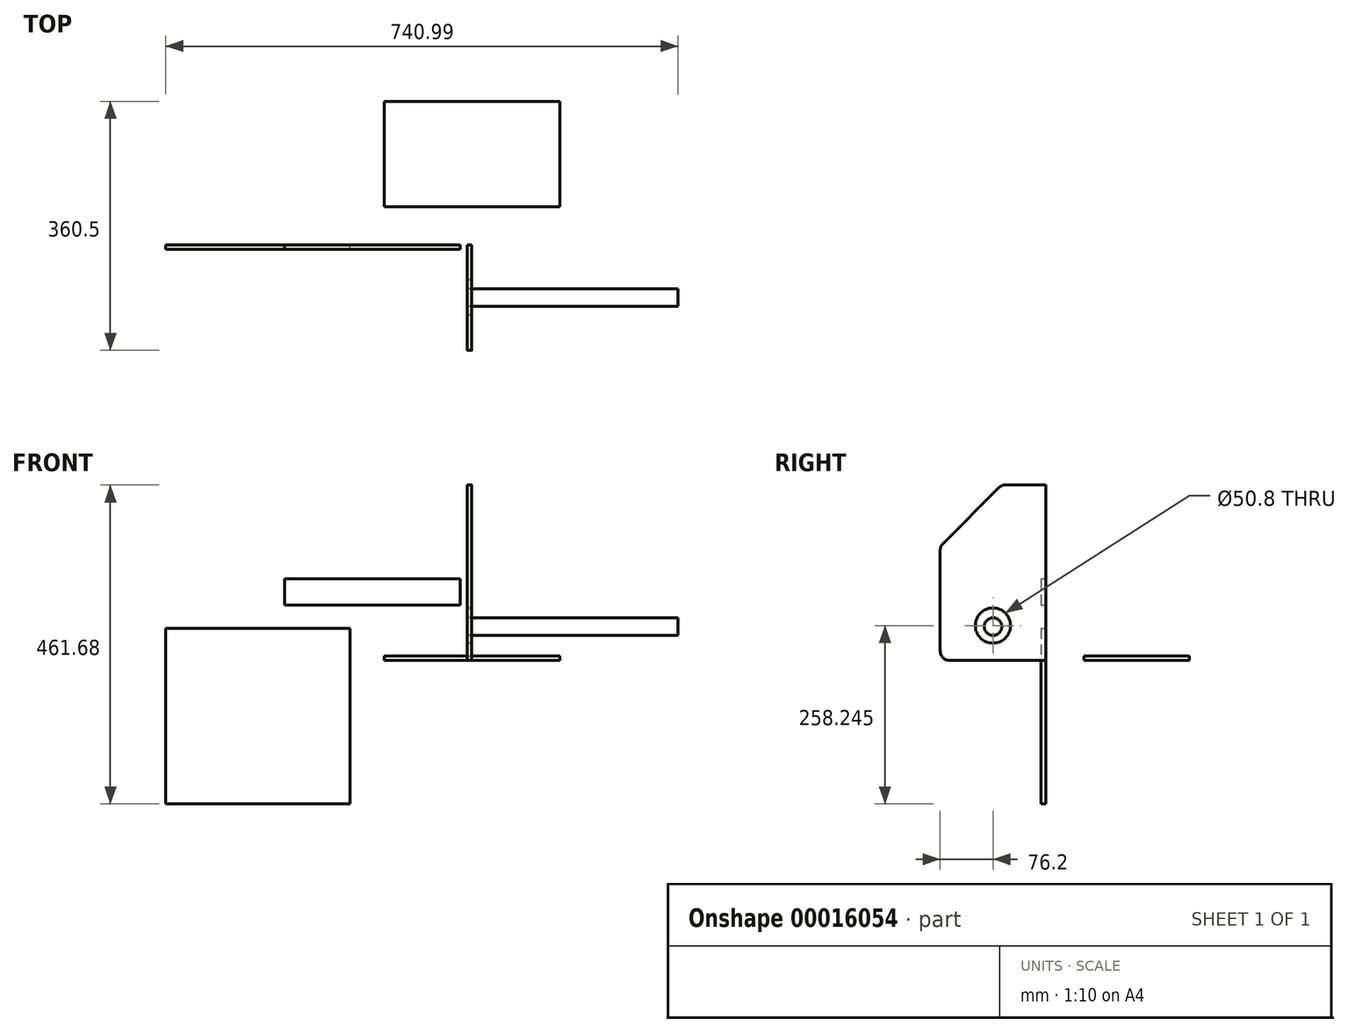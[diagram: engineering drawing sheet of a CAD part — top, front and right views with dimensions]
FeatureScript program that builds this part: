
annotation { "Feature Type Name" : "Feature", "Feature Type Description" : "" }
export const myFeature = defineFeature(function(context is Context, id is Id, definition is map)
    precondition{}
    {
        {
            var Q0;
            Q0=qCreatedBy(makeId("Right.planeOp"),FACE);
            var sketch = newSketch(context, id + "F0", { "sketchPlane" : qUnion([Q0])});
            skLineSegment(sketch, "E0.bottom", {"start": v(0, 0) * mm, "end": v(-138.42, 0) * mm});
            skLineSegment(sketch, "E0.top", {"start": v(0, 254) * mm, "end": v(-63.5, 254) * mm});
            skLineSegment(sketch, "E0.left", {"start": v(0, 0) * mm, "end": v(0, 254) * mm});
            skLineSegment(sketch, "E0.right", {"start": v(-152.4, 13.98) * mm, "end": v(-152.4, 165.1) * mm});
            skLineSegment(sketch, "E1", {"start": v(0, 127) * mm, "end": v(0, 0) * mm});
            skLineSegment(sketch, "E2", {"start": v(-152.4, 127) * mm, "end": v(-152.4, 13.98) * mm});
            skCircle(sketch, "E3", {"center": v(-76.2, 50.57) * mm, "radius": 25.4 * mm});
            skPoint(sketch, "E4.orphan", {"position": v(-152.4, 63.5) * mm});
            skPoint(sketch, "E5.end.orphan", {"position": v(0, 63.5) * mm});
            skPoint(sketch, "E6.orphan", {"position": v(-76.2, 127) * mm});
            skPoint(sketch, "E7.orphan", {"position": v(-76.2, 0) * mm});
            skArc(sketch, "E8", {"start": v(-152.4, 13.98) * mm, "mid": v(-148.3, 4.1) * mm, "end": v(-138.42, 0) * mm});
            skPoint(sketch, "E9.orphan", {"position": v(-152.4, 0) * mm});
            skLineSegment(sketch, "E10", {"start": v(-152.4, 127) * mm, "end": v(-152.4, 165.1) * mm});
            skLineSegment(sketch, "E11", {"start": v(-63.5, 254) * mm, "end": v(-152.4, 165.1) * mm});
            skPoint(sketch, "E12.orphan", {"position": v(-152.4, 254) * mm});
            skSolve(sketch);
        }
        {
            var Q0;
            Q0=makeQuery(id+"F0.imprint","IMPRINT",FACE,{"disambiguationData":[TD([[makeQuery(id+"F0.imprint","IMPRINT",EDGE,{"derivedFrom":sQuery(id+"F0.wireOp",EDGE,"E0.bottom")}),-1.0]])]});
            extrude(context, id + "F1", {"entities" : qUnion([Q0]), "depth" : 6.35 * mm});
        }
        {
            var Q0;
            Q0=makeQuery(id+"F1.opExtrude","SWEPT_EDGE",EDGE,{"disambiguationData":[OSD([sQuery(id+"F0.wireOp",EDGE,"E10"),sQuery(id+"F0.wireOp",EDGE,"E11")])]});
            var Q1;
            Q1=makeQuery(id+"F1.opExtrude","SWEPT_EDGE",EDGE,{"disambiguationData":[OSD([sQuery(id+"F0.wireOp",EDGE,"E0.top"),sQuery(id+"F0.wireOp",EDGE,"E11")])]});
            fillet(context, id + "F2", {"entities" : qUnion([Q0, Q1]), "radius" : 11.17 * mm, "tangentPropagation" : true, "allowEdgeOverflow" : false});
        }
        {
            var Q0;
            Q0=qCreatedBy(makeId("Front.planeOp"),FACE);
            var sketch = newSketch(context, id + "F3", { "sketchPlane" : qUnion([Q0])});
            skLineSegment(sketch, "E13.bottom", {"start": v(-264.59, 118.27) * mm, "end": v(-10.59, 118.27) * mm});
            skLineSegment(sketch, "E13.top", {"start": v(-264.59, 80.17) * mm, "end": v(-10.59, 80.17) * mm});
            skLineSegment(sketch, "E13.left", {"start": v(-264.59, 118.27) * mm, "end": v(-264.59, 80.17) * mm});
            skLineSegment(sketch, "E13.right", {"start": v(-10.59, 118.27) * mm, "end": v(-10.59, 80.17) * mm});
            skSolve(sketch);
        }
        {
            var Q0;
            Q0=makeQuery(id+"F3.imprint","IMPRINT",FACE,{"disambiguationData":[TD([[makeQuery(id+"F3.imprint","IMPRINT",EDGE,{"derivedFrom":sQuery(id+"F3.wireOp",EDGE,"E13.bottom")}),-1.0]])]});
            extrude(context, id + "F4", {"entities" : qUnion([Q0]), "depth" : 6.35 * mm});
        }
        {
            var Q0;
            Q0=qCreatedBy(makeId("Top.planeOp"),FACE);
            var sketch = newSketch(context, id + "F5", { "sketchPlane" : qUnion([Q0])});
            skLineSegment(sketch, "E14.bottom", {"start": v(-120.24, 208.1) * mm, "end": v(133.76, 208.1) * mm});
            skLineSegment(sketch, "E14.top", {"start": v(-120.24, 55.7) * mm, "end": v(133.76, 55.7) * mm});
            skLineSegment(sketch, "E14.left", {"start": v(-120.24, 208.1) * mm, "end": v(-120.24, 55.7) * mm});
            skLineSegment(sketch, "E14.right", {"start": v(133.76, 208.1) * mm, "end": v(133.76, 55.7) * mm});
            skSolve(sketch);
        }
        {
            var Q0;
            Q0=makeQuery(id+"F5.imprint","IMPRINT",FACE,{"disambiguationData":[TD([[makeQuery(id+"F5.imprint","IMPRINT",EDGE,{"derivedFrom":sQuery(id+"F5.wireOp",EDGE,"E14.bottom")}),-1.0]])]});
            extrude(context, id + "F6", {"entities" : qUnion([Q0]), "depth" : 6.35 * mm});
        }
        {
            var Q0;
            Q0=qCreatedBy(makeId("Front.planeOp"),FACE);
            var sketch = newSketch(context, id + "F7", { "sketchPlane" : qUnion([Q0])});
            skLineSegment(sketch, "E15.bottom", {"start": v(-436.19, 46.32) * mm, "end": v(-169.49, 46.32) * mm});
            skLineSegment(sketch, "E15.top", {"start": v(-436.19, -207.68) * mm, "end": v(-169.49, -207.68) * mm});
            skLineSegment(sketch, "E15.left", {"start": v(-436.19, 46.32) * mm, "end": v(-436.19, -207.68) * mm});
            skLineSegment(sketch, "E15.right", {"start": v(-169.49, 46.32) * mm, "end": v(-169.49, -207.68) * mm});
            skSolve(sketch);
        }
        {
            var Q0;
            Q0=makeQuery(id+"F7.imprint","IMPRINT",FACE,{"disambiguationData":[TD([[makeQuery(id+"F7.imprint","IMPRINT",EDGE,{"derivedFrom":sQuery(id+"F7.wireOp",EDGE,"E15.bottom")}),-1.0]])]});
            extrude(context, id + "F8", {"entities" : qUnion([Q0]), "depth" : 6.35 * mm});
        }
        {
            var Q0;
            Q0=qCreatedBy(makeId("Right.planeOp"),FACE);
            var sketch = newSketch(context, id + "F9", { "sketchPlane" : qUnion([Q0])});
            skCircle(sketch, "E16", {"center": v(-76.07, 49.1) * mm, "radius": 12.7 * mm});
            skSolve(sketch);
        }
        {
            var Q0;
            Q0=makeQuery(id+"F9.imprint","IMPRINT",FACE,{"disambiguationData":[TD([[makeQuery(id+"F9.imprint","IMPRINT",EDGE,{"derivedFrom":sQuery(id+"F9.wireOp",EDGE,"E16")}),1.0]])]});
            extrude(context, id + "F10", {"entities" : qUnion([Q0]), "depth" : 304.8 * mm});
        }
    });
